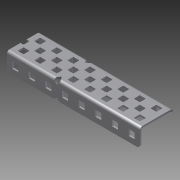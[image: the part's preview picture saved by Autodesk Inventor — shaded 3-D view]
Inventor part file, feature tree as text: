
AUTODESK INVENTOR PART (.ipt)
format: ipt  version: 2014 SP1 (Build 180222100, 222)  size: 791,552 bytes
history: native  units: in
note: dims shown in document units (in); Inventor stores cm internally (conversion verified against a paired STEP export)
features: extrude x2, sketch x2, other x1, imported_body x1
ambient origin geometry x8: Origin, YZ Plane, XZ Plane, XY Plane, X Axis, Y Axis, Z Axis, Center Point
bodies: Body1 (feature_tree)
feature tree (6):
  parser-record x1  (decoder bookkeeping rows leaked as tree rows — omitted from the tree; the rows remain in map.json)
  imported_body  "Base1"
  extrude  "Extrusion1"  Depth=1.0in TaperAngle=0.0deg
  extrude  "Extrusion2"  Depth=0.5in
  sketch  "Sketch2"  dims[d0=1.0in d1=1.0in d2=0.0in]
  sketch  "Sketch4"  dims[d3=0.5in d4=1.0in d5=0.5in d6=1.0in d7=0.0in]
